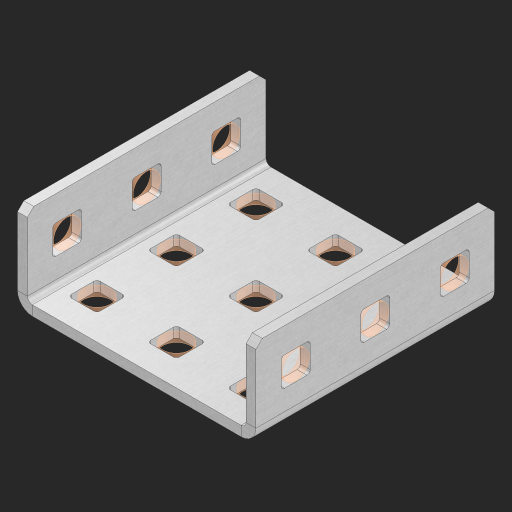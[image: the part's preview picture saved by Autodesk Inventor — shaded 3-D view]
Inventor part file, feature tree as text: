
AUTODESK INVENTOR PART (.ipt)
format: ipt  version: 2023 (Build 270158000, 158)  size: 587,776 bytes
history: native  units: in
note: dims shown in document units (in); Inventor stores cm internally (conversion verified against a paired STEP export)
features: other x20, extrude x14, sheet_metal_op x10, sketch x8, mirror x1, pattern_linear x1, chamfer x1
ambient origin geometry x8: Origin, YZ Plane, XZ Plane, XY Plane, X Axis, Y Axis, Z Axis, Center Point
bodies: Solid1 (feature_tree), Body (feature_tree)
feature tree (55):
  other  "Flange Pattern Plane"
  sheet_metal_op  "Flange Pattern"
  sheet_metal_op  "Body Pattern"
  other  "Arc Length"
  mirror  "Notch Mirror"
  pattern_linear  "Notch Pattern"  Spacing1=0.25in  [1 undecoded]
  chamfer  "End Chamfer"
  extrude  "Half Cut"  Depth=0.0625in
  sketch  "Sketch1"  dims[d0=1.5in]
  other  "Plate1"
  sketch  "Sketch2"  dims[d1=1.5in]
  other  "Plate2"
  sheet_metal_op  "Bend1"
  sheet_metal_op  "Corner1"
  sketch  "Sketch3"  dims[d2=0.0625in]
  other  "Flange Pattern Sketch"
  sketch  "Sketch7"  dims[d3=0.0625in]
  other  "Srf1"
  other  "Srf2"
  sketch  "Sketch8"  dims[d4=0.0312in]
  sketch  "Sketch9"  dims[d5=0.125in]
  other  "Srf91"
  sheet_metal_op  "Body Pattern Sketch"
  other  "Srf92"
  sketch  "Sketch13"  dims[d6=0.0625in]
  sketch  "Sketch14"  dims[d7=0.5in d8=90.0deg d9=0.0312in d10=0.25in d11=0.0625in d12=0.0625in d16=0.182in d17=0.02in d18=0.0625in d19=0.0in d20=0.25in d21=0.25in d46=0.172in d47=1.0in d48=0.0in d49=0.182in d50=0.02in d51=0.25in d52=0.25in d53=0.0625in d54=0.0in d55=0.172in d56=1.0in d57=0.0in d60=1.1811in d62=0.5in d63=1.1811in d65=0.5in d85=0.1473in d86=0.1782in d88=0.04in d89=0.0625in d90=0.0in d91=0.04in d92=0.0491in d95=2.5in d96=0.04in d97=0.25in d98=45.0deg d101=0.0in d102=2.497in d131=1.5in d132=1.1811in d134=0.5in d139=0.5in]
  other  "Srf856"
  other  "Srf1310"
  other  "Srf1311"
  other  "Srf1312"
  other  "Srf1376"
  other  "Srf1377"
  other  "Srf1728"
  other  "Srf1755"
  other  "Srf1942"
  other  "Srf1943"
  other  "Srf1944"
  sheet_metal_op  "Flange Stamp"
  sheet_metal_op  "Flange Circle"
  sheet_metal_op  "Body Stamp"
  sheet_metal_op  "Body Circle"
  sheet_metal_op  "Notch"
  extrude  "ExtrusionSrf2"  Depth=0.0625in
  extrude  "ExtrusionSrf92"  Depth=0.182in
  extrude  "ExtrusionSrf856"  Depth=0.02in
  extrude  "ExtrusionSrf1310"  Depth=0.0625in
  extrude  "ExtrusionSrf1311"  TaperAngle=0.0deg  [1 undecoded]
  extrude  "ExtrusionSrf1312"  Depth=0.25in
  extrude  "ExtrusionSrf1376"  Depth=0.25in
  extrude  "ExtrusionSrf1377"  Depth=0.5in
  extrude  "ExtrusionSrf1728"  Depth=1.0in TaperAngle=0.0deg
  extrude  "ExtrusionSrf1755"  Depth=0.182in
  extrude  "ExtrusionSrf1942"  Depth=0.02in
  extrude  "ExtrusionSrf1943"  Depth=0.25in
  extrude  "ExtrusionSrf1944"  Depth=0.25in
note: 2 required parameter values undecoded (feature->parameter linkage not recoverable at this tier; creation-order binding heuristic only, values carry confidence <= 0.55)
